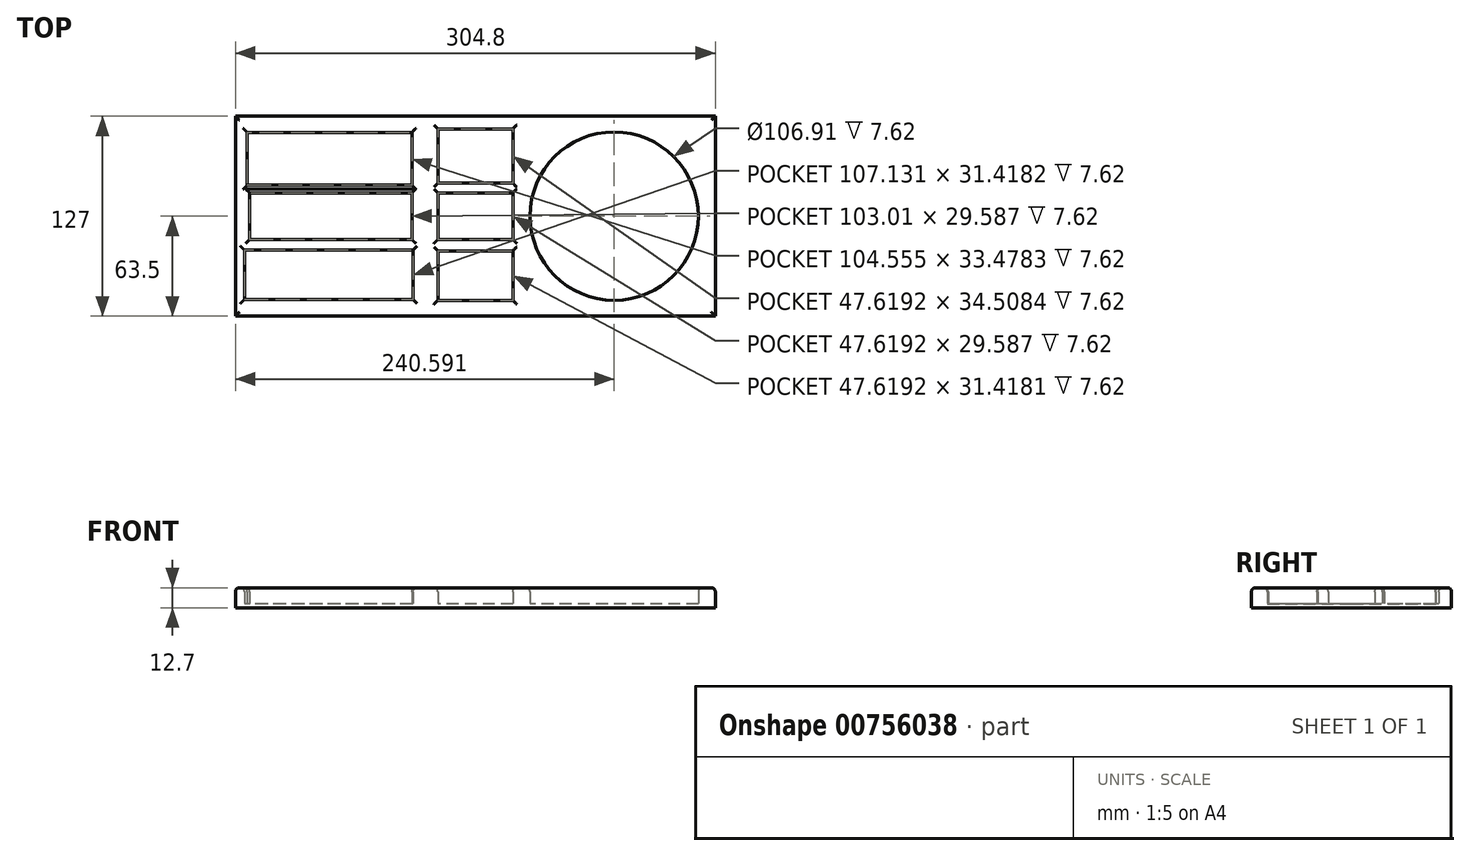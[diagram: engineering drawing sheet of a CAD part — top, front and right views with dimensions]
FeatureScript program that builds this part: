
annotation { "Feature Type Name" : "Feature", "Feature Type Description" : "" }
export const myFeature = defineFeature(function(context is Context, id is Id, definition is map)
    precondition{}
    {
        {
            var Q0;
            Q0=qCreatedBy(makeId("Top.planeOp"),FACE);
            var sketch = newSketch(context, id + "F0", { "sketchPlane" : qUnion([Q0])});
            skLineSegment(sketch, "E0.bottom", {"start": v(152.4, 63.5) * mm, "end": v(-152.4, 63.5) * mm});
            skLineSegment(sketch, "E0.top", {"start": v(152.4, -63.5) * mm, "end": v(-152.4, -63.5) * mm});
            skLineSegment(sketch, "E0.left", {"start": v(152.4, 63.5) * mm, "end": v(152.4, -63.5) * mm});
            skLineSegment(sketch, "E0.right", {"start": v(-152.4, 63.5) * mm, "end": v(-152.4, -63.5) * mm});
            skPoint(sketch, "E0.middle", {"position": v(0, 0) * mm});
            skLineSegment(sketch, "E1.bottom", {"start": v(-39.54, -21.52) * mm, "end": v(-146.67, -21.52) * mm});
            skLineSegment(sketch, "E1.top", {"start": v(-39.54, -52.94) * mm, "end": v(-146.67, -52.94) * mm});
            skLineSegment(sketch, "E1.left", {"start": v(-39.54, -21.52) * mm, "end": v(-39.54, -52.94) * mm});
            skLineSegment(sketch, "E1.right", {"start": v(-146.67, -21.52) * mm, "end": v(-146.67, -52.94) * mm});
            skPoint(sketch, "E1.middle", {"position": v(-93.1, -37.23) * mm});
            skLineSegment(sketch, "E2.bottom", {"start": v(-40.31, 14.8) * mm, "end": v(-143.32, 14.8) * mm});
            skLineSegment(sketch, "E2.top", {"start": v(-40.31, -14.8) * mm, "end": v(-143.32, -14.8) * mm});
            skLineSegment(sketch, "E2.left", {"start": v(-40.31, 14.8) * mm, "end": v(-40.31, -14.8) * mm});
            skLineSegment(sketch, "E2.right", {"start": v(-143.32, 14.8) * mm, "end": v(-143.32, -14.8) * mm});
            skPoint(sketch, "E2.middle", {"position": v(-91.82, 0) * mm});
            skLineSegment(sketch, "E3.bottom", {"start": v(-40.31, 53.16) * mm, "end": v(-144.87, 53.16) * mm});
            skLineSegment(sketch, "E3.top", {"start": v(-40.31, 19.69) * mm, "end": v(-144.87, 19.69) * mm});
            skLineSegment(sketch, "E3.left", {"start": v(-40.31, 53.16) * mm, "end": v(-40.31, 19.69) * mm});
            skLineSegment(sketch, "E3.right", {"start": v(-144.87, 53.16) * mm, "end": v(-144.87, 19.69) * mm});
            skPoint(sketch, "E3.middle", {"position": v(-92.6, 36.43) * mm});
            skLineSegment(sketch, "E4.bottom", {"start": v(23.8, 55.48) * mm, "end": v(-23.8, 55.48) * mm});
            skLineSegment(sketch, "E4.top", {"start": v(23.8, 20.97) * mm, "end": v(-23.8, 20.97) * mm});
            skLineSegment(sketch, "E4.left", {"start": v(23.8, 55.48) * mm, "end": v(23.8, 20.97) * mm});
            skLineSegment(sketch, "E4.right", {"start": v(-23.8, 55.48) * mm, "end": v(-23.8, 20.97) * mm});
            skPoint(sketch, "E4.middle", {"position": v(0, 38.23) * mm});
            skLineSegment(sketch, "E5.bottom", {"start": v(23.8, 14.8) * mm, "end": v(-23.8, 14.8) * mm});
            skLineSegment(sketch, "E5.top", {"start": v(23.8, -14.8) * mm, "end": v(-23.8, -14.8) * mm});
            skLineSegment(sketch, "E5.left", {"start": v(23.8, 14.8) * mm, "end": v(23.8, -14.8) * mm});
            skLineSegment(sketch, "E5.right", {"start": v(-23.8, 14.8) * mm, "end": v(-23.8, -14.8) * mm});
            skLineSegment(sketch, "E6.bottom", {"start": v(23.8, -22.03) * mm, "end": v(-23.8, -22.03) * mm});
            skLineSegment(sketch, "E6.top", {"start": v(23.8, -53.45) * mm, "end": v(-23.8, -53.45) * mm});
            skLineSegment(sketch, "E6.left", {"start": v(23.8, -22.03) * mm, "end": v(23.8, -53.45) * mm});
            skLineSegment(sketch, "E6.right", {"start": v(-23.8, -22.03) * mm, "end": v(-23.8, -53.45) * mm});
            skPoint(sketch, "E6.middle", {"position": v(0, -37.74) * mm});
            skCircle(sketch, "E7", {"center": v(88.2, 0) * mm, "radius": 53.46 * mm});
            skSolve(sketch);
        }
        {
            var Q0;
            Q0 = qSketchRegion(id + "F0", true);
            extrude(context, id + "F1", {"entities" : qUnion([Q0]), "depth" : 12.7 * mm, "offsetDistance" : 25.4 * mm});
        }
        {
            var Q0;
            Q0=makeQuery(id+"F0.imprint","IMPRINT",FACE,{"disambiguationData":[TD([[makeQuery(id+"F0.imprint","IMPRINT",EDGE,{"derivedFrom":sQuery(id+"F0.wireOp",EDGE,"E3.bottom")}),1.0]])]});
            var Q1;
            Q1=makeQuery(id+"F0.imprint","IMPRINT",FACE,{"disambiguationData":[TD([[makeQuery(id+"F0.imprint","IMPRINT",EDGE,{"derivedFrom":sQuery(id+"F0.wireOp",EDGE,"E2.bottom")}),1.0]])]});
            var Q2;
            Q2=makeQuery(id+"F0.imprint","IMPRINT",FACE,{"disambiguationData":[TD([[makeQuery(id+"F0.imprint","IMPRINT",EDGE,{"derivedFrom":sQuery(id+"F0.wireOp",EDGE,"E1.bottom")}),1.0]])]});
            var Q3;
            Q3=makeQuery(id+"F0.imprint","IMPRINT",FACE,{"disambiguationData":[TD([[makeQuery(id+"F0.imprint","IMPRINT",EDGE,{"derivedFrom":sQuery(id+"F0.wireOp",EDGE,"E6.bottom")}),1.0]])]});
            var Q4;
            Q4=makeQuery(id+"F0.imprint","IMPRINT",FACE,{"disambiguationData":[TD([[makeQuery(id+"F0.imprint","IMPRINT",EDGE,{"derivedFrom":sQuery(id+"F0.wireOp",EDGE,"E5.bottom")}),1.0]])]});
            var Q5;
            Q5=makeQuery(id+"F0.imprint","IMPRINT",FACE,{"disambiguationData":[TD([[makeQuery(id+"F0.imprint","IMPRINT",EDGE,{"derivedFrom":sQuery(id+"F0.wireOp",EDGE,"E4.bottom")}),1.0]])]});
            var Q6;
            Q6=makeQuery(id+"F0.imprint","IMPRINT",FACE,{"disambiguationData":[TD([[makeQuery(id+"F0.imprint","IMPRINT",EDGE,{"derivedFrom":sQuery(id+"F0.wireOp",EDGE,"E7")}),1.0]])]});
            extrude(context, id + "F2", {"entities" : qUnion([Q0, Q1, Q2, Q3, Q4, Q5, Q6]), "operationType" : NewBodyOperationType.ADD, "depth" : 2.54 * mm, "offsetDistance" : 25.4 * mm});
        }
        {
            var Q0;
            Q0=makeQuery(id+"F2.opExtrude","CAP_EDGE",EDGE,{"disambiguationData":[OSD([sQuery(id+"F0.wireOp",EDGE,"E3.bottom")])],"isStart":false});
            var Q1;
            Q1=makeQuery(id+"F2.opExtrude","CAP_EDGE",EDGE,{"disambiguationData":[OSD([sQuery(id+"F0.wireOp",EDGE,"E3.left")])],"isStart":false});
            var Q2;
            Q2=makeQuery(id+"F2.opExtrude","CAP_EDGE",EDGE,{"disambiguationData":[OSD([sQuery(id+"F0.wireOp",EDGE,"E3.right")])],"isStart":false});
            var Q3;
            Q3=makeQuery(id+"F2.opExtrude","CAP_EDGE",EDGE,{"disambiguationData":[OSD([sQuery(id+"F0.wireOp",EDGE,"E3.top")])],"isStart":false});
            var Q4;
            Q4=makeQuery(id+"F2.opExtrude","CAP_EDGE",EDGE,{"disambiguationData":[OSD([sQuery(id+"F0.wireOp",EDGE,"E2.bottom")])],"isStart":false});
            var Q5;
            Q5=makeQuery(id+"F2.opExtrude","CAP_EDGE",EDGE,{"disambiguationData":[OSD([sQuery(id+"F0.wireOp",EDGE,"E2.right")])],"isStart":false});
            var Q6;
            Q6=makeQuery(id+"F2.opExtrude","CAP_EDGE",EDGE,{"disambiguationData":[OSD([sQuery(id+"F0.wireOp",EDGE,"E2.left")])],"isStart":false});
            var Q7;
            Q7=makeQuery(id+"F2.opExtrude","CAP_EDGE",EDGE,{"disambiguationData":[OSD([sQuery(id+"F0.wireOp",EDGE,"E2.top")])],"isStart":false});
            var Q8;
            Q8=makeQuery(id+"F2.opExtrude","CAP_EDGE",EDGE,{"disambiguationData":[OSD([sQuery(id+"F0.wireOp",EDGE,"E1.bottom")])],"isStart":false});
            var Q9;
            Q9=makeQuery(id+"F2.opExtrude","CAP_EDGE",EDGE,{"disambiguationData":[OSD([sQuery(id+"F0.wireOp",EDGE,"E5.bottom")])],"isStart":false});
            var Q10;
            Q10=makeQuery(id+"F2.opExtrude","CAP_EDGE",EDGE,{"disambiguationData":[OSD([sQuery(id+"F0.wireOp",EDGE,"E6.bottom")])],"isStart":false});
            var Q11;
            Q11=makeQuery(id+"F2.opExtrude","CAP_EDGE",EDGE,{"disambiguationData":[OSD([sQuery(id+"F0.wireOp",EDGE,"E4.bottom")])],"isStart":false});
            var Q12;
            Q12=makeQuery(id+"F2.opExtrude","CAP_EDGE",EDGE,{"disambiguationData":[OSD([sQuery(id+"F0.wireOp",EDGE,"E1.top")])],"isStart":false});
            var Q13;
            Q13=makeQuery(id+"F2.opExtrude","CAP_EDGE",EDGE,{"disambiguationData":[OSD([sQuery(id+"F0.wireOp",EDGE,"E6.top")])],"isStart":false});
            var Q14;
            Q14=makeQuery(id+"F2.opExtrude","CAP_EDGE",EDGE,{"disambiguationData":[OSD([sQuery(id+"F0.wireOp",EDGE,"E5.top")])],"isStart":false});
            var Q15;
            Q15=makeQuery(id+"F2.opExtrude","CAP_EDGE",EDGE,{"disambiguationData":[OSD([sQuery(id+"F0.wireOp",EDGE,"E1.left")])],"isStart":false});
            var Q16;
            Q16=makeQuery(id+"F2.opExtrude","CAP_EDGE",EDGE,{"disambiguationData":[OSD([sQuery(id+"F0.wireOp",EDGE,"E1.right")])],"isStart":false});
            var Q17;
            Q17=makeQuery(id+"F2.opExtrude","CAP_EDGE",EDGE,{"disambiguationData":[OSD([sQuery(id+"F0.wireOp",EDGE,"E6.left")])],"isStart":false});
            var Q18;
            Q18=makeQuery(id+"F2.opExtrude","CAP_EDGE",EDGE,{"disambiguationData":[OSD([sQuery(id+"F0.wireOp",EDGE,"E5.left")])],"isStart":false});
            var Q19;
            Q19=makeQuery(id+"F2.opExtrude","CAP_EDGE",EDGE,{"disambiguationData":[OSD([sQuery(id+"F0.wireOp",EDGE,"E4.left")])],"isStart":false});
            var Q20;
            Q20=makeQuery(id+"F2.opExtrude","CAP_EDGE",EDGE,{"disambiguationData":[OSD([sQuery(id+"F0.wireOp",EDGE,"E4.right")])],"isStart":false});
            var Q21;
            Q21=makeQuery(id+"F2.opExtrude","CAP_EDGE",EDGE,{"disambiguationData":[OSD([sQuery(id+"F0.wireOp",EDGE,"E5.right")])],"isStart":false});
            var Q22;
            Q22=makeQuery(id+"F2.opExtrude","CAP_EDGE",EDGE,{"disambiguationData":[OSD([sQuery(id+"F0.wireOp",EDGE,"E6.right")])],"isStart":false});
            var Q23;
            Q23=makeQuery(id+"F2.opExtrude","CAP_EDGE",EDGE,{"disambiguationData":[OSD([sQuery(id+"F0.wireOp",EDGE,"E7")])],"isStart":false});
            var Q24;
            Q24=makeQuery(id+"F1.opExtrude","CAP_EDGE",EDGE,{"disambiguationData":[OSD([sQuery(id+"F0.wireOp",EDGE,"E7")])],"isStart":false});
            var Q25;
            Q25=makeQuery(id+"F1.opExtrude","CAP_EDGE",EDGE,{"disambiguationData":[OSD([sQuery(id+"F0.wireOp",EDGE,"E4.bottom")])],"isStart":false});
            var Q26;
            Q26=makeQuery(id+"F1.opExtrude","CAP_EDGE",EDGE,{"disambiguationData":[OSD([sQuery(id+"F0.wireOp",EDGE,"E5.bottom")])],"isStart":false});
            var Q27;
            Q27=makeQuery(id+"F1.opExtrude","CAP_EDGE",EDGE,{"disambiguationData":[OSD([sQuery(id+"F0.wireOp",EDGE,"E3.top")])],"isStart":false});
            var Q28;
            Q28=makeQuery(id+"F1.opExtrude","CAP_EDGE",EDGE,{"disambiguationData":[OSD([sQuery(id+"F0.wireOp",EDGE,"E3.bottom")])],"isStart":false});
            var Q29;
            Q29=makeQuery(id+"F1.opExtrude","CAP_EDGE",EDGE,{"disambiguationData":[OSD([sQuery(id+"F0.wireOp",EDGE,"E3.left")])],"isStart":false});
            var Q30;
            Q30=makeQuery(id+"F1.opExtrude","CAP_EDGE",EDGE,{"disambiguationData":[OSD([sQuery(id+"F0.wireOp",EDGE,"E3.right")])],"isStart":false});
            var Q31;
            Q31=makeQuery(id+"F1.opExtrude","CAP_EDGE",EDGE,{"disambiguationData":[OSD([sQuery(id+"F0.wireOp",EDGE,"E1.bottom")])],"isStart":false});
            var Q32;
            Q32=makeQuery(id+"F1.opExtrude","CAP_EDGE",EDGE,{"disambiguationData":[OSD([sQuery(id+"F0.wireOp",EDGE,"E1.right")])],"isStart":false});
            var Q33;
            Q33=makeQuery(id+"F1.opExtrude","CAP_EDGE",EDGE,{"disambiguationData":[OSD([sQuery(id+"F0.wireOp",EDGE,"E1.top")])],"isStart":false});
            var Q34;
            Q34=makeQuery(id+"F1.opExtrude","CAP_EDGE",EDGE,{"disambiguationData":[OSD([sQuery(id+"F0.wireOp",EDGE,"E1.left")])],"isStart":false});
            var Q35;
            Q35=makeQuery(id+"F1.opExtrude","CAP_EDGE",EDGE,{"disambiguationData":[OSD([sQuery(id+"F0.wireOp",EDGE,"E4.left")])],"isStart":false});
            var Q36;
            Q36=makeQuery(id+"F1.opExtrude","CAP_EDGE",EDGE,{"disambiguationData":[OSD([sQuery(id+"F0.wireOp",EDGE,"E5.left")])],"isStart":false});
            var Q37;
            Q37=makeQuery(id+"F1.opExtrude","CAP_EDGE",EDGE,{"disambiguationData":[OSD([sQuery(id+"F0.wireOp",EDGE,"E6.left")])],"isStart":false});
            var Q38;
            Q38=makeQuery(id+"F1.opExtrude","CAP_EDGE",EDGE,{"disambiguationData":[OSD([sQuery(id+"F0.wireOp",EDGE,"E6.bottom")])],"isStart":false});
            var Q39;
            Q39=makeQuery(id+"F1.opExtrude","CAP_EDGE",EDGE,{"disambiguationData":[OSD([sQuery(id+"F0.wireOp",EDGE,"E5.top")])],"isStart":false});
            var Q40;
            Q40=makeQuery(id+"F1.opExtrude","CAP_EDGE",EDGE,{"disambiguationData":[OSD([sQuery(id+"F0.wireOp",EDGE,"E4.top")])],"isStart":false});
            var Q41;
            Q41=makeQuery(id+"F1.opExtrude","CAP_EDGE",EDGE,{"disambiguationData":[OSD([sQuery(id+"F0.wireOp",EDGE,"E6.right")])],"isStart":false});
            var Q42;
            Q42=makeQuery(id+"F1.opExtrude","CAP_EDGE",EDGE,{"disambiguationData":[OSD([sQuery(id+"F0.wireOp",EDGE,"E6.top")])],"isStart":false});
            var Q43;
            Q43=makeQuery(id+"F1.opExtrude","CAP_FACE",FACE,{"disambiguationData":[OSD([sQuery(id+"F0.wireOp",EDGE,"E0.bottom"),sQuery(id+"F0.wireOp",EDGE,"E0.top"),sQuery(id+"F0.wireOp",EDGE,"E0.left"),sQuery(id+"F0.wireOp",EDGE,"E0.right"),sQuery(id+"F0.wireOp",EDGE,"E1.bottom"),sQuery(id+"F0.wireOp",EDGE,"E1.top"),sQuery(id+"F0.wireOp",EDGE,"E1.left"),sQuery(id+"F0.wireOp",EDGE,"E1.right"),sQuery(id+"F0.wireOp",EDGE,"E2.bottom"),sQuery(id+"F0.wireOp",EDGE,"E2.top"),sQuery(id+"F0.wireOp",EDGE,"E2.left"),sQuery(id+"F0.wireOp",EDGE,"E2.right"),sQuery(id+"F0.wireOp",EDGE,"E3.bottom"),sQuery(id+"F0.wireOp",EDGE,"E3.top"),sQuery(id+"F0.wireOp",EDGE,"E3.left"),sQuery(id+"F0.wireOp",EDGE,"E3.right"),sQuery(id+"F0.wireOp",EDGE,"E4.bottom"),sQuery(id+"F0.wireOp",EDGE,"E4.top"),sQuery(id+"F0.wireOp",EDGE,"E4.left"),sQuery(id+"F0.wireOp",EDGE,"E4.right"),sQuery(id+"F0.wireOp",EDGE,"E5.bottom"),sQuery(id+"F0.wireOp",EDGE,"E5.top"),sQuery(id+"F0.wireOp",EDGE,"E5.left"),sQuery(id+"F0.wireOp",EDGE,"E5.right"),sQuery(id+"F0.wireOp",EDGE,"E6.bottom"),sQuery(id+"F0.wireOp",EDGE,"E6.top"),sQuery(id+"F0.wireOp",EDGE,"E6.left"),sQuery(id+"F0.wireOp",EDGE,"E6.right"),sQuery(id+"F0.wireOp",EDGE,"E7")])],"isStart":false});
            var Q44;
            Q44=makeQuery(id+"F1.opExtrude","CAP_EDGE",EDGE,{"disambiguationData":[OSD([sQuery(id+"F0.wireOp",EDGE,"E5.right")])],"isStart":false});
            fillet(context, id + "F3", {"entities" : qUnion([Q0, Q1, Q2, Q3, Q4, Q5, Q6, Q7, Q8, Q9, Q10, Q11, Q12, Q13, Q14, Q15, Q16, Q17, Q18, Q19, Q20, Q21, Q22, Q23, Q24, Q25, Q26, Q27, Q28, Q29, Q30, Q31, Q32, Q33, Q34, Q35, Q36, Q37, Q38, Q39, Q40, Q41, Q42, Q43, Q44]), "radius" : 2.54 * mm, "tangentPropagation" : true, "allowEdgeOverflow" : false});
        }
    });
